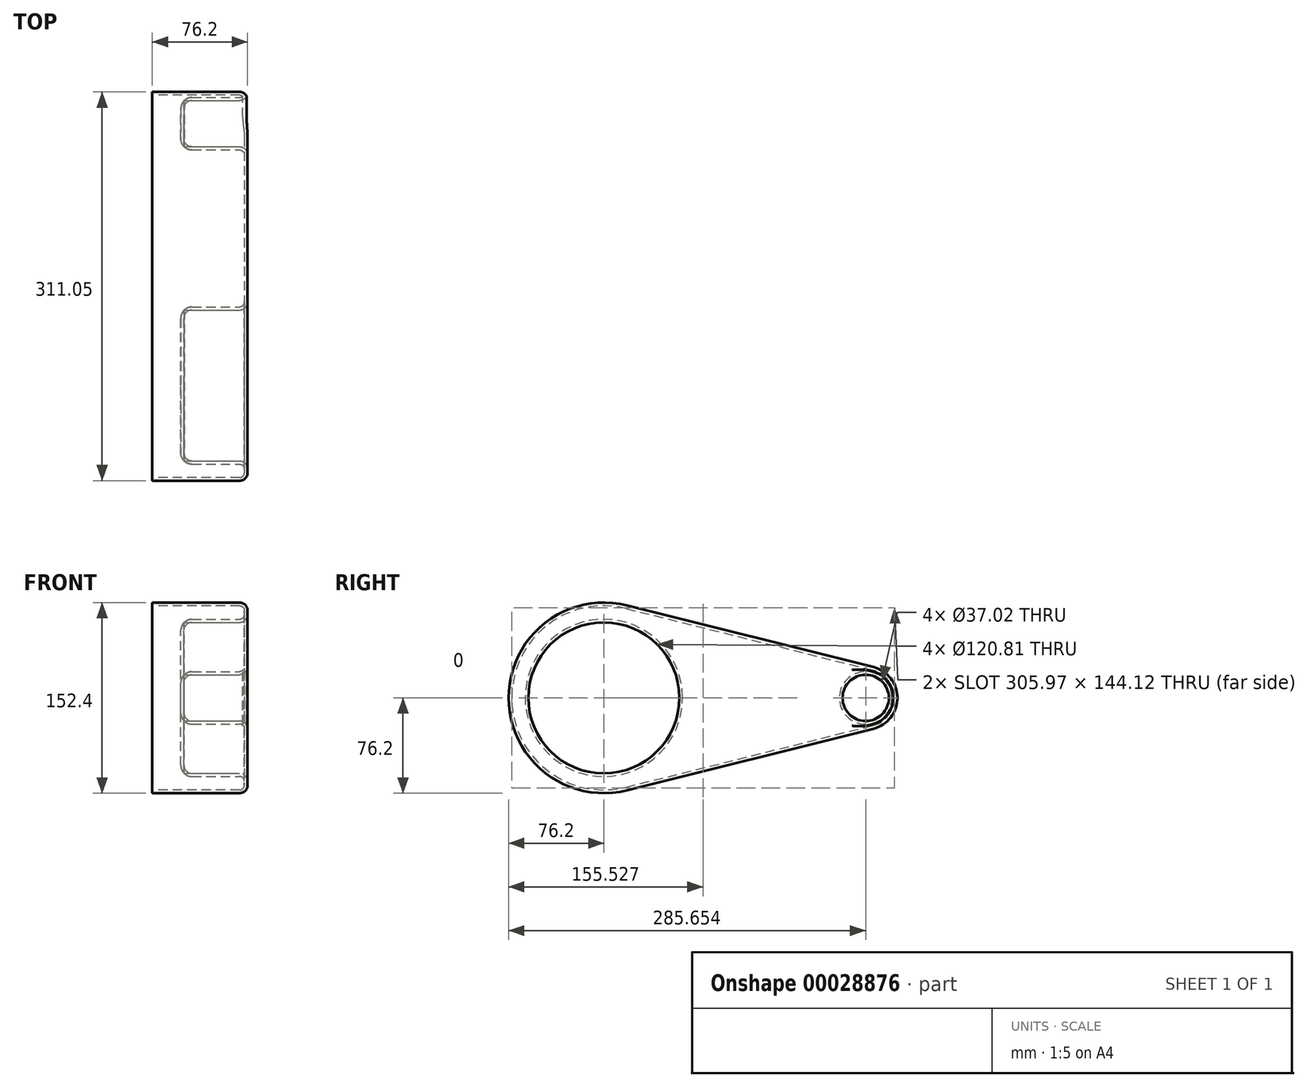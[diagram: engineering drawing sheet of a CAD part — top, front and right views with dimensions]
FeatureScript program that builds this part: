
annotation { "Feature Type Name" : "Feature", "Feature Type Description" : "" }
export const myFeature = defineFeature(function(context is Context, id is Id, definition is map)
    precondition{}
    {
        {
            var Q0;
            Q0=qCreatedBy(makeId("Right.planeOp"),FACE);
            var sketch = newSketch(context, id + "F0", { "sketchPlane" : qUnion([Q0])});
            skCircle(sketch, "E0", {"center": v(0, 0) * mm, "radius": 76.2 * mm});
            skCircle(sketch, "E1", {"center": v(209.45, 0) * mm, "radius": 25.4 * mm});
            skLineSegment(sketch, "E2", {"start": v(18.48, 73.92) * mm, "end": v(215.61, 24.64) * mm});
            skLineSegment(sketch, "E3", {"start": v(18.48, -73.92) * mm, "end": v(215.61, -24.64) * mm});
            skSolve(sketch);
        }
        {
            var Q0;
            {var subQ0=sQuery(id+"F0.wireOp",EDGE,"E0");var subQ2=makeQuery(id+"F0.imprint","INTERSECT",VERTEX,{"derivedFrom":[subQ0,sQuery(id+"F0.wireOp",EDGE,"E2")]});Q0=makeQuery(id+"F0.imprint","IMPRINT",FACE,{"disambiguationData":[TD([[makeQuery(id+"F0.imprint","IMPRINT",EDGE,{"disambiguationData":[TD([[subQ2,-1.0]])],"derivedFrom":subQ0}),1.0]])]});}
            var Q1;
            {var subQ1=sQuery(id+"F0.wireOp",EDGE,"E2");Q1=makeQuery(id+"F0.imprint","IMPRINT",FACE,{"disambiguationData":[TD([[makeQuery(id+"F0.imprint","IMPRINT",EDGE,{"derivedFrom":subQ1}),-1.0]])]});}
            var Q2;
            {var subQ0=sQuery(id+"F0.wireOp",EDGE,"E1");var subQ2=makeQuery(id+"F0.imprint","INTERSECT",VERTEX,{"derivedFrom":[subQ0,sQuery(id+"F0.wireOp",EDGE,"E2")]});Q2=makeQuery(id+"F0.imprint","IMPRINT",FACE,{"disambiguationData":[TD([[makeQuery(id+"F0.imprint","IMPRINT",EDGE,{"disambiguationData":[TD([[subQ2,-1.0]])],"derivedFrom":subQ0}),1.0]])]});}
            extrude(context, id + "F1", {"entities" : qUnion([Q0, Q1, Q2]), "depth" : 76.2 * mm});
        }
        {
            var Q0;
            Q0=makeQuery(id+"F1.opExtrude","CAP_FACE",FACE,{"disambiguationData":[OSD([sQuery(id+"F0.wireOp",EDGE,"E0"),sQuery(id+"F0.wireOp",EDGE,"E1"),sQuery(id+"F0.wireOp",EDGE,"E2"),sQuery(id+"F0.wireOp",EDGE,"E3")])],"isStart":false});
            var sketch = newSketch(context, id + "F2", { "sketchPlane" : qUnion([Q0])});
            skCircle(sketch, "E4", {"center": v(0, 0) * mm, "radius": 60.4 * mm});
            skCircle(sketch, "E5", {"center": v(209.45, 0) * mm, "radius": 18.51 * mm});
            skSolve(sketch);
        }
        {
            var Q0;
            Q0=makeQuery(id+"F2.imprint","IMPRINT",FACE,{"disambiguationData":[TD([[makeQuery(id+"F2.imprint","IMPRINT",EDGE,{"derivedFrom":sQuery(id+"F2.wireOp",EDGE,"E4")}),1.0]])]});
            var Q1;
            Q1=makeQuery(id+"F2.imprint","IMPRINT",FACE,{"disambiguationData":[TD([[makeQuery(id+"F2.imprint","IMPRINT",EDGE,{"derivedFrom":sQuery(id+"F2.wireOp",EDGE,"E5")}),1.0]])]});
            extrude(context, id + "F3", {"entities" : qUnion([Q0, Q1]), "operationType" : NewBodyOperationType.REMOVE, "oppositeDirection" : true, "depth" : 50.8 * mm});
        }
        {
            var Q0;
            Q0=makeQuery(id+"F1.opExtrude","CAP_FACE",FACE,{"disambiguationData":[OSD([sQuery(id+"F0.wireOp",EDGE,"E0"),sQuery(id+"F0.wireOp",EDGE,"E1"),sQuery(id+"F0.wireOp",EDGE,"E2"),sQuery(id+"F0.wireOp",EDGE,"E3")])],"isStart":false});
            var Q1;
            Q1=makeQuery(id+"F3.boolean.opBoolean","COPY",EDGE,{"derivedFrom":makeQuery(id+"F3.opExtrude","CAP_EDGE",EDGE,{"disambiguationData":[OSD([sQuery(id+"F2.wireOp",EDGE,"E4")])],"isStart":false})});
            var Q2;
            Q2=makeQuery(id+"F3.boolean.opBoolean","COPY",EDGE,{"derivedFrom":makeQuery(id+"F3.opExtrude","CAP_EDGE",EDGE,{"disambiguationData":[OSD([sQuery(id+"F2.wireOp",EDGE,"E5")])],"isStart":true})});
            var Q3;
            Q3=makeQuery(id+"F3.boolean.opBoolean","COPY",EDGE,{"derivedFrom":makeQuery(id+"F3.opExtrude","CAP_EDGE",EDGE,{"disambiguationData":[OSD([sQuery(id+"F2.wireOp",EDGE,"E5")])],"isStart":false})});
            fillet(context, id + "F4", {"entities" : qUnion([Q0, Q1, Q2, Q3]), "radius" : 6.35 * mm, "tangentPropagation" : true, "allowEdgeOverflow" : false});
        }
        {
            var Q0;
            Q0=makeQuery(id+"F1.opExtrude","CAP_FACE",FACE,{"disambiguationData":[OSD([sQuery(id+"F0.wireOp",EDGE,"E0"),sQuery(id+"F0.wireOp",EDGE,"E1"),sQuery(id+"F0.wireOp",EDGE,"E2"),sQuery(id+"F0.wireOp",EDGE,"E3")])],"isStart":true});
            shell(context, id + "F5", {"entities" : qUnion([Q0]), "thickness" : 2.54 * mm});
        }
    });
